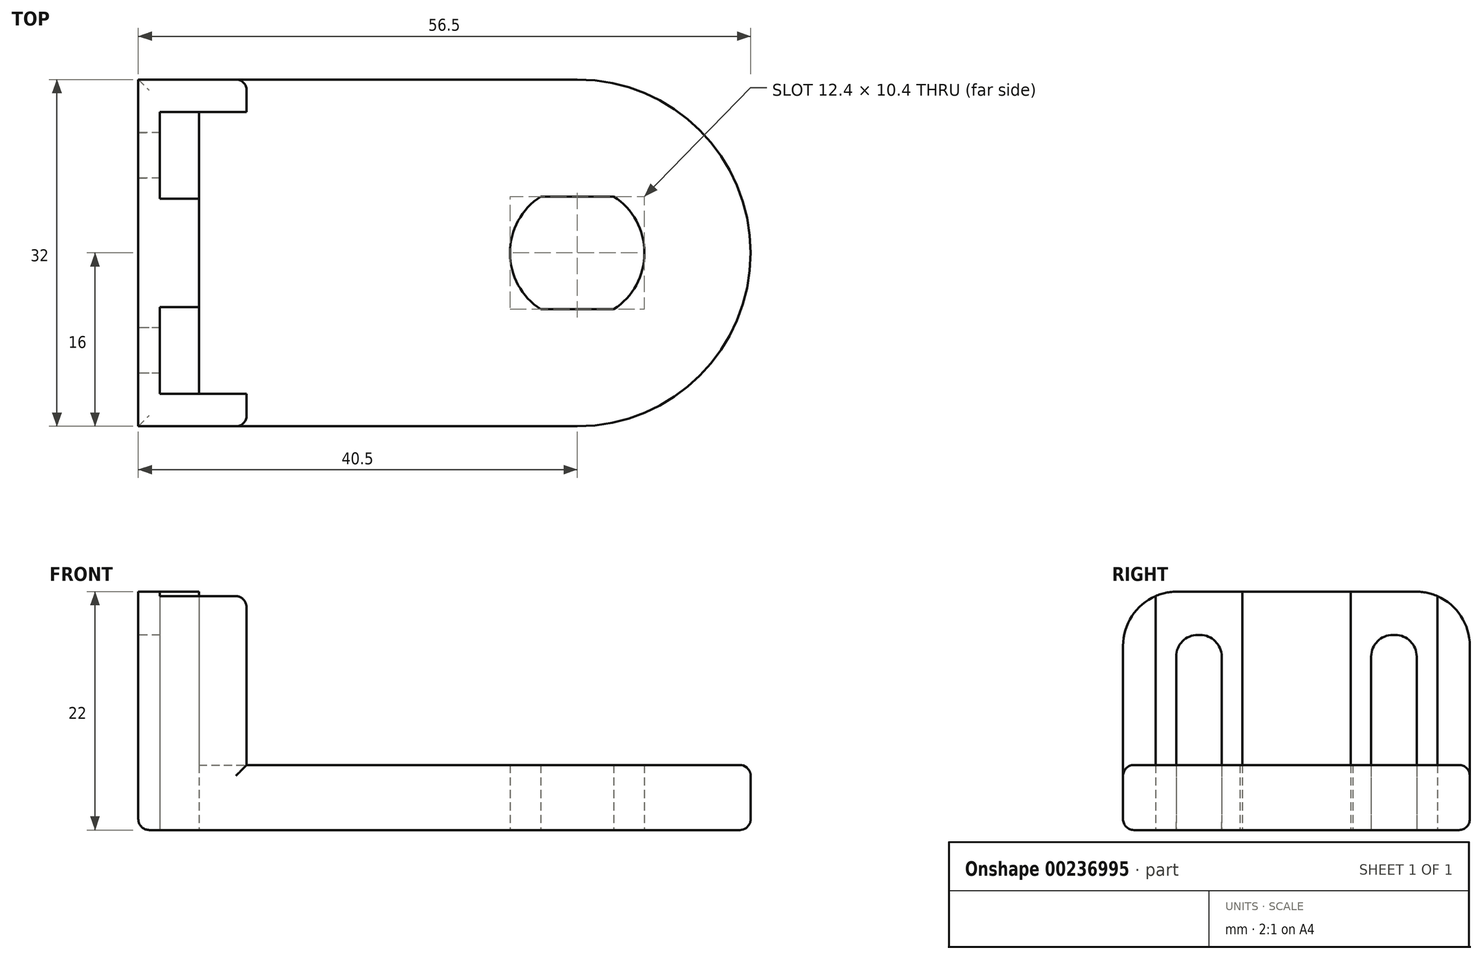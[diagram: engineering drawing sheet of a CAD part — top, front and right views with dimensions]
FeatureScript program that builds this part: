
annotation { "Feature Type Name" : "Feature", "Feature Type Description" : "" }
export const myFeature = defineFeature(function(context is Context, id is Id, definition is map)
    precondition{}
    {
        {
            var Q0;
            Q0=qCreatedBy(makeId("Top.planeOp"),FACE);
            var sketch = newSketch(context, id + "F0", { "sketchPlane" : qUnion([Q0])});
            skCircle(sketch, "E0", {"center": v(0, 0) * mm, "radius": 16 * mm});
            skLineSegment(sketch, "E1.bottom", {"start": v(0, -16) * mm, "end": v(-40.5, -16) * mm});
            skLineSegment(sketch, "E1.top", {"start": v(0, 16) * mm, "end": v(-40.5, 16) * mm});
            skLineSegment(sketch, "E1.left", {"start": v(0, -16) * mm, "end": v(0, 16) * mm});
            skLineSegment(sketch, "E1.right", {"start": v(-40.5, -16) * mm, "end": v(-40.5, 16) * mm});
            skSolve(sketch);
        }
        {
            var Q0;
            Q0 = qSketchRegion(id + "F0", true);
            extrude(context, id + "F1", {"entities" : qUnion([Q0]), "depth" : 6 * mm});
        }
        {
            var Q0;
            Q0=qCreatedBy(makeId("Top.planeOp"),FACE);
            var sketch = newSketch(context, id + "F2", { "sketchPlane" : qUnion([Q0])});
            skLineSegment(sketch, "E2.bottom", {"start": v(-40.5, 16) * mm, "end": v(-30.5, 16) * mm});
            skLineSegment(sketch, "E2.top", {"start": v(-40.5, -16) * mm, "end": v(-30.5, -16) * mm});
            skLineSegment(sketch, "E2.left", {"start": v(-40.5, 16) * mm, "end": v(-40.5, -16) * mm});
            skLineSegment(sketch, "E2.right", {"start": v(-30.5, 16) * mm, "end": v(-30.5, -16) * mm});
            skSolve(sketch);
        }
        {
            var Q0;
            Q0 = qSketchRegion(id + "F2", true);
            extrude(context, id + "F3", {"entities" : qUnion([Q0]), "operationType" : NewBodyOperationType.ADD, "depth" : 22 * mm});
        }
        {
            var Q0;
            Q0=qCreatedBy(makeId("Top.planeOp"),FACE);
            var sketch = newSketch(context, id + "F4", { "sketchPlane" : qUnion([Q0])});
            skLineSegment(sketch, "E3.bottom", {"start": v(-38.5, 13) * mm, "end": v(-34.9, 13) * mm});
            skLineSegment(sketch, "E3.top", {"start": v(-38.5, 5) * mm, "end": v(-34.9, 5) * mm});
            skLineSegment(sketch, "E3.left", {"start": v(-38.5, 13) * mm, "end": v(-38.5, 5) * mm});
            skLineSegment(sketch, "E3.right", {"start": v(-34.9, 13) * mm, "end": v(-34.9, 5) * mm});
            skLineSegment(sketch, "E4.bottom", {"start": v(-38.5, 11.1) * mm, "end": v(-40.5, 11.1) * mm});
            skLineSegment(sketch, "E4.top", {"start": v(-38.5, 6.9) * mm, "end": v(-40.5, 6.9) * mm});
            skLineSegment(sketch, "E4.left", {"start": v(-38.5, 11.1) * mm, "end": v(-38.5, 6.9) * mm});
            skLineSegment(sketch, "E4.right", {"start": v(-40.5, 11.1) * mm, "end": v(-40.5, 6.9) * mm});
            skSolve(sketch);
        }
        {
            var Q0;
            Q0 = qSketchRegion(id + "F4", true);
            extrude(context, id + "F5", {"entities" : qUnion([Q0]), "operationType" : NewBodyOperationType.REMOVE, "depth" : 18 * mm});
        }
        {
            var Q0;
            Q0=makeQuery(id+"F5.boolean.opBoolean","COPY",EDGE,{"derivedFrom":makeQuery(id+"F5.opExtrude","CAP_EDGE",EDGE,{"disambiguationData":[OSD([sQuery(id+"F4.wireOp",EDGE,"E4.top")])],"isStart":false})});
            var Q1;
            Q1=makeQuery(id+"F5.boolean.opBoolean","COPY",EDGE,{"derivedFrom":makeQuery(id+"F5.opExtrude","CAP_EDGE",EDGE,{"disambiguationData":[OSD([sQuery(id+"F4.wireOp",EDGE,"E4.bottom")])],"isStart":false})});
            fillet(context, id + "F6", {"entities" : qUnion([Q0, Q1]), "radius" : 2 * mm, "tangentPropagation" : true, "allowEdgeOverflow" : false});
        }
        {
            var Q0;
            Q0=makeQuery(id+"F1.opExtrude","SWEPT_BODY",BODY,{"disambiguationData":[OSD([sQuery(id+"F0.wireOp",EDGE,"E0"),sQuery(id+"F0.wireOp",EDGE,"E1.bottom"),sQuery(id+"F0.wireOp",EDGE,"E1.top"),sQuery(id+"F0.wireOp",EDGE,"E1.right")])]});
            var Q1;
            Q1=qCreatedBy(makeId("Front.planeOp"),FACE);
            mirror(context, id + "F7", {"operationType" : NewBodyOperationType.INTERSECT, "entities" : qUnion([Q0]), "mirrorPlane" : qUnion([Q1])});
        }
        {
            var Q0;
            Q0=qCreatedBy(makeId("Top.planeOp"),FACE);
            cPlane(context, id + "F8", {"entities" : qUnion([Q0]), "cplaneType" : CPlaneType.OFFSET, "offset" : 6 * mm, "width" : 150 * mm, "height" : 150 * mm});
        }
        {
            var Q0;
            Q0=qCreatedBy(id+"F8.planeOp",FACE);
            var sketch = newSketch(context, id + "F9", { "sketchPlane" : qUnion([Q0])});
            skLineSegment(sketch, "E5.bottom", {"start": v(-38.5, 13) * mm, "end": v(-30.5, 13) * mm});
            skLineSegment(sketch, "E5.top", {"start": v(-38.5, -13) * mm, "end": v(-30.5, -13) * mm});
            skLineSegment(sketch, "E5.left", {"start": v(-38.5, 13) * mm, "end": v(-38.5, -13) * mm});
            skLineSegment(sketch, "E5.right", {"start": v(-30.5, 13) * mm, "end": v(-30.5, -13) * mm});
            skLineSegment(sketch, "E6.bottom", {"start": v(-38.5, -5) * mm, "end": v(-34.9, -5) * mm});
            skLineSegment(sketch, "E6.top", {"start": v(-38.5, 5) * mm, "end": v(-34.9, 5) * mm});
            skLineSegment(sketch, "E6.left", {"start": v(-38.5, -5) * mm, "end": v(-38.5, 5) * mm});
            skLineSegment(sketch, "E6.right", {"start": v(-34.9, -5) * mm, "end": v(-34.9, 5) * mm});
            skSolve(sketch);
        }
        {
            var Q0;
            {var subQ4=sQuery(id+"F9.wireOp",EDGE,"E5.bottom");Q0=makeQuery(id+"F9.imprint","IMPRINT",FACE,{"disambiguationData":[TD([[makeQuery(id+"F9.imprint","IMPRINT",EDGE,{"derivedFrom":subQ4}),-1.0]])]});}
            var Q1;
            Q1=sQuery(id+"F9.wireOp",EDGE,"E6.right");
            var Q2;
            Q2=sQuery(id+"F9.wireOp",EDGE,"E6.top");
            var Q3;
            Q3=sQuery(id+"F9.wireOp",EDGE,"E6.bottom");
            var Q4;
            Q4=sQuery(id+"F9.wireOp",EDGE,"E5.right");
            var Q5;
            Q5=sQuery(id+"F9.wireOp",EDGE,"E5.top");
            var Q6;
            Q6=sQuery(id+"F9.wireOp",EDGE,"E5.bottom");
            extrude(context, id + "F10", {"entities" : qUnion([Q0]), "operationType" : NewBodyOperationType.REMOVE, "surfaceEntities" : qUnion([Q1, Q2, Q3, Q4, Q5, Q6]), "depth" : 25 * mm});
        }
        {
            var Q0;
            Q0=qCreatedBy(makeId("Top.planeOp"),FACE);
            var sketch = newSketch(context, id + "F11", { "sketchPlane" : qUnion([Q0])});
            skCircle(sketch, "E7", {"center": v(0, 0) * mm, "radius": 6 * mm});
            skLineSegment(sketch, "E8", {"start": v(3.32, 5) * mm, "end": v(-3.32, 5) * mm});
            skLineSegment(sketch, "E9", {"start": v(3.32, -5) * mm, "end": v(-3.32, -5) * mm});
            skSolve(sketch);
        }
        {
            var Q0;
            {var subQ0=sQuery(id+"F11.wireOp",EDGE,"E8");Q0=makeQuery(id+"F11.imprint","IMPRINT",FACE,{"disambiguationData":[TD([[makeQuery(id+"F11.imprint","IMPRINT",EDGE,{"derivedFrom":subQ0}),1.0]])]});}
            var sketch = newSketch(context, id + "F12", { "sketchPlane" : qUnion([Q0])});
            skArc(sketch, "E10.0", {"start": v(3.38, -5.2) * mm, "mid": v(6.2, 0) * mm, "end": v(3.38, 5.2) * mm});
            skLineSegment(sketch, "E10.1", {"start": v(-3.38, -5.2) * mm, "end": v(3.38, -5.2) * mm});
            skArc(sketch, "E10.2", {"start": v(-3.38, 5.2) * mm, "mid": v(-6.2, 0) * mm, "end": v(-3.38, -5.2) * mm});
            skLineSegment(sketch, "E10.3", {"start": v(3.38, 5.2) * mm, "end": v(-3.38, 5.2) * mm});
            skSolve(sketch);
        }
        {
            var Q0;
            Q0 = qSketchRegion(id + "F12", true);
            extrude(context, id + "F13", {"entities" : qUnion([Q0]), "operationType" : NewBodyOperationType.REMOVE, "depth" : 25 * mm});
        }
        {
            var Q0;
            Q0=makeQuery(id+"F3.opExtrude","CAP_EDGE",EDGE,{"disambiguationData":[OSD([sQuery(id+"F2.wireOp",EDGE,"E2.bottom")])],"isStart":false});
            var Q1;
            Q1=makeQuery(id+"F3.opExtrude","CAP_EDGE",EDGE,{"disambiguationData":[OSD([sQuery(id+"F2.wireOp",EDGE,"E2.top")])],"isStart":false});
            fillet(context, id + "F14", {"entities" : qUnion([Q0, Q1]), "radius" : 5 * mm, "tangentPropagation" : true, "allowEdgeOverflow" : false});
        }
        {
            var Q0;
            Q0=makeQuery(id+"F1.opExtrude","CAP_EDGE",EDGE,{"disambiguationData":[OSD([sQuery(id+"F0.wireOp",EDGE,"E1.top")])],"isStart":false});
            var Q1;
            Q1=makeQuery(id+"F1.opExtrude","CAP_EDGE",EDGE,{"disambiguationData":[OSD([sQuery(id+"F0.wireOp",EDGE,"E0")])],"isStart":false});
            var Q2;
            Q2=makeQuery(id+"F1.opExtrude","CAP_EDGE",EDGE,{"disambiguationData":[OSD([sQuery(id+"F0.wireOp",EDGE,"E1.bottom")])],"isStart":false});
            var Q3;
            Q3=makeQuery(id+"F3.opExtrude","SWEPT_EDGE",EDGE,{"disambiguationData":[OSD([sQuery(id+"F2.wireOp",EDGE,"E2.top"),sQuery(id+"F2.wireOp",EDGE,"E2.right")])]});
            var Q4;
            Q4=makeQuery(id+"F3.opExtrude","SWEPT_EDGE",EDGE,{"disambiguationData":[OSD([sQuery(id+"F2.wireOp",EDGE,"E2.bottom"),sQuery(id+"F2.wireOp",EDGE,"E2.right")])]});
            fillet(context, id + "F15", {"entities" : qUnion([Q0, Q1, Q2, Q3, Q4]), "radius" : 1 * mm, "tangentPropagation" : true, "allowEdgeOverflow" : false});
        }
        {
            var Q0;
            Q0=makeQuery(id+"F1.opExtrude","CAP_EDGE",EDGE,{"disambiguationData":[OSD([sQuery(id+"F0.wireOp",EDGE,"E1.top")])],"isStart":true});
            var Q1;
            {var subQ0=makeQuery(id+"F5.opExtrude","SWEPT_FACE",FACE,{"disambiguationData":[OSD([sQuery(id+"F4.wireOp",EDGE,"E4.top")])]});var subQ1=makeQuery(id+"F5.boolean.opBoolean","COPY",FACE,{"derivedFrom":subQ0});var subQ2=sQuery(id+"F0.wireOp",EDGE,"E1.right");var subQ5=sQuery(id+"F0.wireOp",EDGE,"E1.bottom");Q1=makeQuery(id+"F7.boolean.opBoolean","SPLIT",EDGE,{"disambiguationData":[TD([subQ1])],"derivedFrom":makeQuery(id+"F5.boolean.opBoolean","SPLIT",EDGE,{"disambiguationData":[TD([makeQuery(id+"F1.opExtrude","SWEPT_FACE",FACE,{"disambiguationData":[OSD([subQ5])]})])],"derivedFrom":makeQuery(id+"F1.opExtrude","CAP_EDGE",EDGE,{"disambiguationData":[OSD([subQ2])],"isStart":true})})});}
            var Q2;
            {var subQ0=sQuery(id+"F0.wireOp",EDGE,"E1.right");var subQ1=sQuery(id+"F0.wireOp",EDGE,"E1.top");Q2=makeQuery(id+"F5.boolean.opBoolean","SPLIT",EDGE,{"disambiguationData":[TD([makeQuery(id+"F1.opExtrude","SWEPT_FACE",FACE,{"disambiguationData":[OSD([subQ1])]})])],"derivedFrom":makeQuery(id+"F1.opExtrude","CAP_EDGE",EDGE,{"disambiguationData":[OSD([subQ0])],"isStart":true})});}
            var Q3;
            {var subQ1=sQuery(id+"F0.wireOp",EDGE,"E1.right");var subQ3=sQuery(id+"F0.wireOp",EDGE,"E1.bottom");var subQ4=makeQuery(id+"F1.opExtrude","SWEPT_FACE",FACE,{"disambiguationData":[OSD([subQ3])]});Q3=makeQuery(id+"F7.boolean.opBoolean","SPLIT",EDGE,{"disambiguationData":[TD([subQ4])],"derivedFrom":makeQuery(id+"F5.boolean.opBoolean","SPLIT",EDGE,{"disambiguationData":[TD([subQ4])],"derivedFrom":makeQuery(id+"F1.opExtrude","CAP_EDGE",EDGE,{"disambiguationData":[OSD([subQ1])],"isStart":true})})});}
            fillet(context, id + "F16", {"entities" : qUnion([Q0, Q1, Q2, Q3]), "radius" : 1 * mm, "tangentPropagation" : true, "allowEdgeOverflow" : false});
        }
    });
